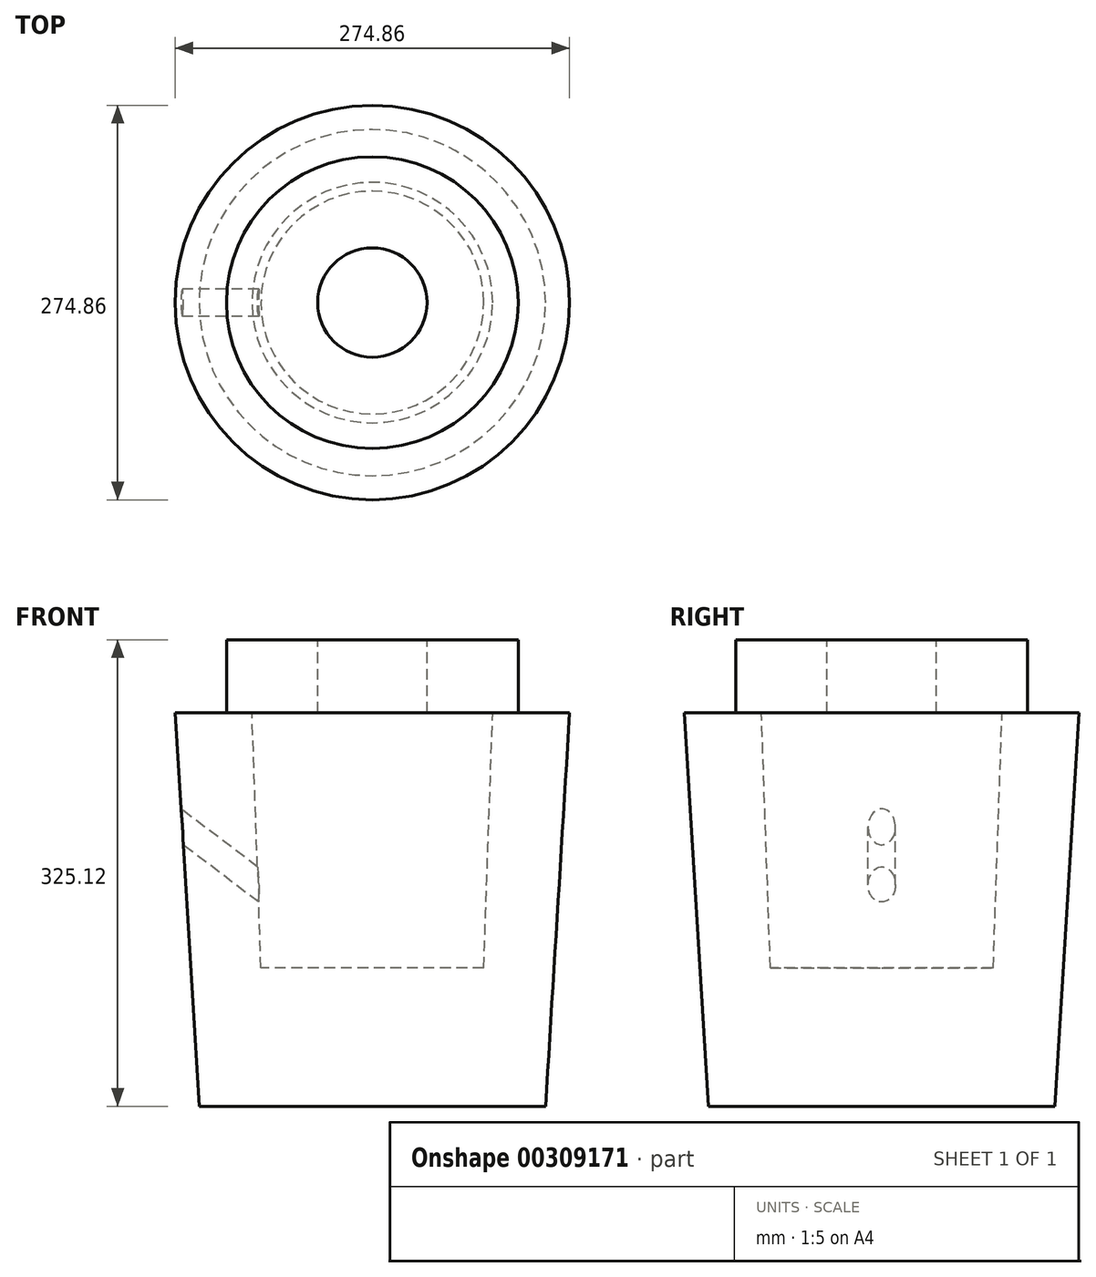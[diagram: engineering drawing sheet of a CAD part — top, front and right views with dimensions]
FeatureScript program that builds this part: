
annotation { "Feature Type Name" : "Feature", "Feature Type Description" : "" }
export const myFeature = defineFeature(function(context is Context, id is Id, definition is map)
    precondition{}
    {
        {
            var Q0;
            Q0=qCreatedBy(makeId("Top.planeOp"),FACE);
            var sketch = newSketch(context, id + "F0", { "sketchPlane" : qUnion([Q0])});
            skCircle(sketch, "E0", {"center": v(0, 0) * mm, "radius": 120.65 * mm});
            skSolve(sketch);
        }
        {
            var Q0;
            Q0=makeQuery(id+"F0.imprint","IMPRINT",FACE,{"disambiguationData":[TD([[makeQuery(id+"F0.imprint","IMPRINT",EDGE,{"derivedFrom":sQuery(id+"F0.wireOp",EDGE,"E0")}),1.0]])]});
            extrude(context, id + "F1", {"entities" : qUnion([Q0]), "depth" : 274.32 * mm, "hasDraft" : true, "draftAngle" : 3.5 * degree});
        }
        {
            var Q0;
            Q0=makeQuery(id+"F1.opExtrude","CAP_FACE",FACE,{"disambiguationData":[OSD([sQuery(id+"F0.wireOp",EDGE,"E0")])],"isStart":false});
            var sketch = newSketch(context, id + "F2", { "sketchPlane" : qUnion([Q0])});
            skCircle(sketch, "E1", {"center": v(0, 0) * mm, "radius": 137.16 * mm});
            skSolve(sketch);
        }
        {
            var Q0;
            Q0=makeQuery(id+"F2.imprint","IMPRINT",FACE,{"disambiguationData":[TD([[makeQuery(id+"F2.imprint","IMPRINT",EDGE,{"derivedFrom":sQuery(id+"F2.wireOp",EDGE,"E1")}),1.0]])]});
            var sketch = newSketch(context, id + "F3", { "sketchPlane" : qUnion([Q0])});
            skCircle(sketch, "E2", {"center": v(0, 0) * mm, "radius": 83.82 * mm});
            skSolve(sketch);
        }
        {
            var Q0;
            Q0 = qSketchRegion(id + "F3", true);
            extrude(context, id + "F4", {"entities" : qUnion([Q0]), "operationType" : NewBodyOperationType.REMOVE, "oppositeDirection" : true, "depth" : 177.8 * mm, "hasDraft" : true, "draftAngle" : 2 * degree, "draftPullDirection" : true});
        }
        {
            var Q0;
            Q0=qCreatedBy(makeId("Front.planeOp"),FACE);
            var sketch = newSketch(context, id + "F5", { "sketchPlane" : qUnion([Q0])});
            skLineSegment(sketch, "E3", {"start": v(-160, 203.6) * mm, "end": v(-38.61, 111.47) * mm});
            skLineSegment(sketch, "E4", {"start": v(-38.61, 111.47) * mm, "end": v(-27.1, 126.64) * mm});
            skLineSegment(sketch, "E5", {"start": v(-27.1, 126.64) * mm, "end": v(-148.49, 218.78) * mm});
            skLineSegment(sketch, "E6", {"start": v(-148.49, 218.78) * mm, "end": v(-160, 203.6) * mm});
            skLineSegment(sketch, "E7", {"start": v(-154.25, 211.2) * mm, "end": v(-32.85, 119.05) * mm});
            skSolve(sketch);
        }
        {
            var Q0;
            {var subQ0=sQuery(id+"F5.wireOp",EDGE,"E3");Q0=makeQuery(id+"F5.imprint","IMPRINT",FACE,{"disambiguationData":[TD([[makeQuery(id+"F5.imprint","IMPRINT",EDGE,{"derivedFrom":subQ0}),1.0]])]});}
            var Q1;
            Q1=sQuery(id+"F5.wireOp",EDGE,"E7");
            revolve(context, id + "F6", {"operationType" : NewBodyOperationType.REMOVE, "entities" : qUnion([Q0]), "axis" : qUnion([Q1]), "revolveType" : RevolveType.FULL});
        }
        {
            var Q0;
            Q0=makeQuery(id+"F2.imprint","IMPRINT",FACE,{"disambiguationData":[TD([[makeQuery(id+"F2.imprint","IMPRINT",EDGE,{"derivedFrom":sQuery(id+"F2.wireOp",EDGE,"E1")}),1.0]])]});
            var sketch = newSketch(context, id + "F7", { "sketchPlane" : qUnion([Q0])});
            skCircle(sketch, "E8", {"center": v(0, 0) * mm, "radius": 101.6 * mm});
            skSolve(sketch);
        }
        {
            var Q0;
            Q0 = qSketchRegion(id + "F7", true);
            extrude(context, id + "F8", {"entities" : qUnion([Q0]), "depth" : 50.8 * mm});
        }
        {
            var Q0;
            Q0=makeQuery(id+"F8.opExtrude","CAP_FACE",FACE,{"disambiguationData":[OSD([sQuery(id+"F7.wireOp",EDGE,"E8")])],"isStart":false});
            var sketch = newSketch(context, id + "F9", { "sketchPlane" : qUnion([Q0])});
            skCircle(sketch, "E9", {"center": v(0, 0) * mm, "radius": 38.1 * mm});
            skSolve(sketch);
        }
        {
            var Q0;
            Q0=makeQuery(id+"F9.imprint","IMPRINT",FACE,{"disambiguationData":[TD([[makeQuery(id+"F9.imprint","IMPRINT",EDGE,{"derivedFrom":sQuery(id+"F9.wireOp",EDGE,"E9")}),1.0]])]});
            extrude(context, id + "F10", {"entities" : qUnion([Q0]), "operationType" : NewBodyOperationType.REMOVE, "oppositeDirection" : true, "depth" : 50.8 * mm});
        }
    });
